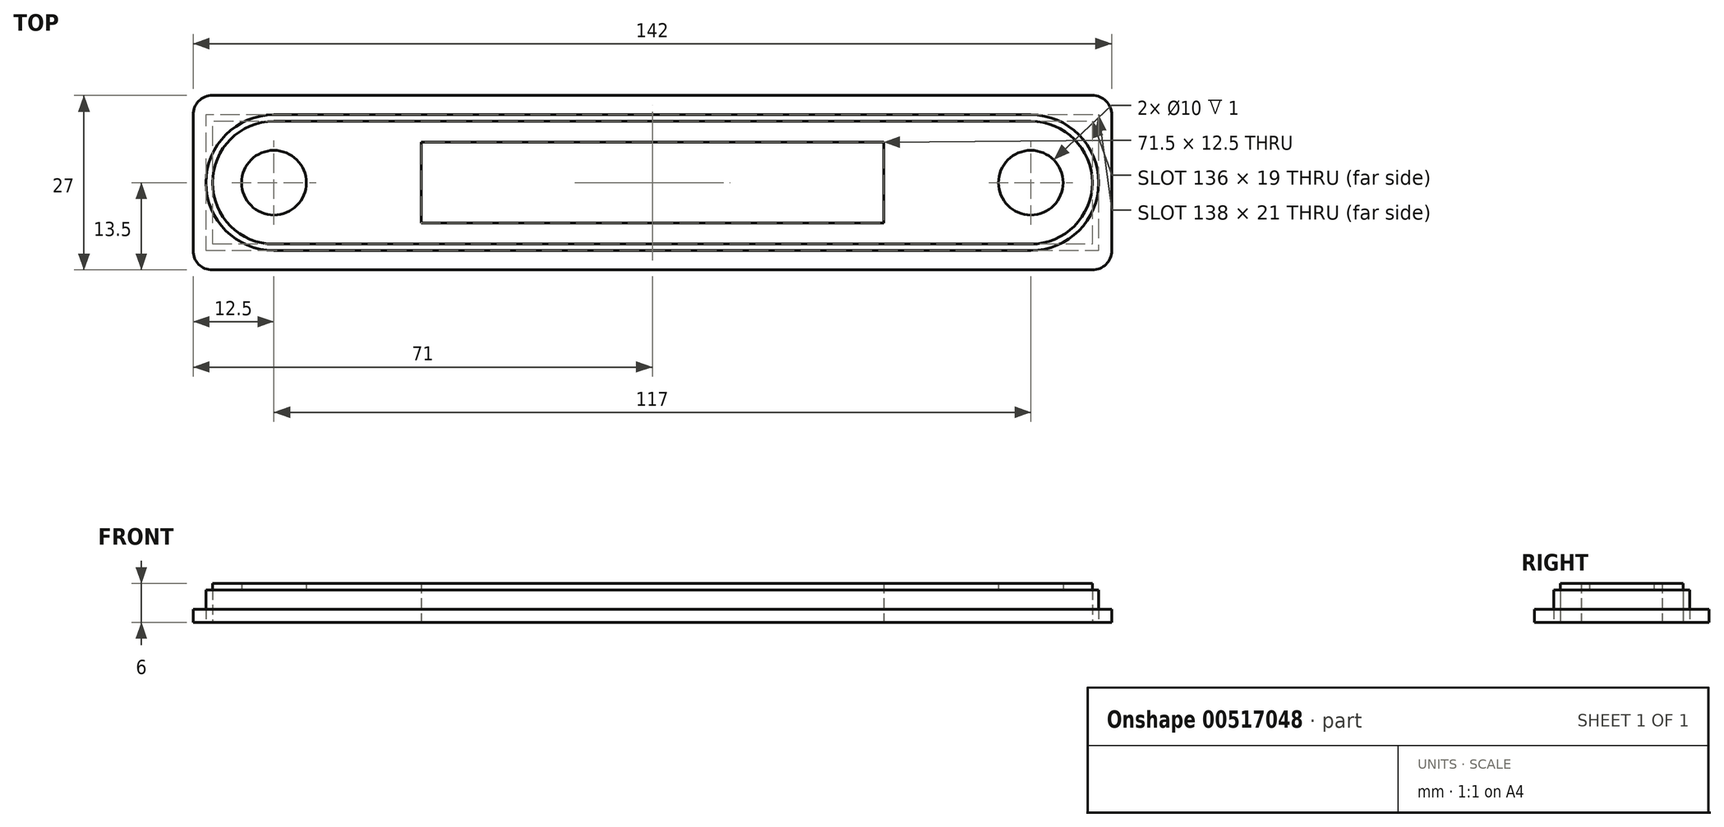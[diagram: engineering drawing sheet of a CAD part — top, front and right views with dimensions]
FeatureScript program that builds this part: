
annotation { "Feature Type Name" : "Feature", "Feature Type Description" : "" }
export const myFeature = defineFeature(function(context is Context, id is Id, definition is map)
    precondition{}
    {
        {
            var Q0;
            Q0=qCreatedBy(makeId("Top.planeOp"),FACE);
            var sketch = newSketch(context, id + "F0", { "sketchPlane" : qUnion([Q0])});
            skArc(sketch, "E0", {"start": v(-58.5, 5) * mm, "mid": v(-62.04, 3.54) * mm, "end": v(-63.5, 0) * mm});
            skArc(sketch, "E1", {"start": v(-63.5, 0) * mm, "mid": v(-62.04, -3.54) * mm, "end": v(-58.5, -5) * mm});
            skArc(sketch, "E2", {"start": v(-58.5, -5) * mm, "mid": v(-54.96, -3.54) * mm, "end": v(-53.5, 0) * mm});
            skArc(sketch, "E3", {"start": v(-53.5, 0) * mm, "mid": v(-54.96, 3.54) * mm, "end": v(-58.5, 5) * mm});
            skArc(sketch, "E4", {"start": v(58.5, 5) * mm, "mid": v(54.96, 3.54) * mm, "end": v(53.5, 0) * mm});
            skArc(sketch, "E5", {"start": v(53.5, 0) * mm, "mid": v(54.96, -3.54) * mm, "end": v(58.5, -5) * mm});
            skArc(sketch, "E6", {"start": v(58.5, -5) * mm, "mid": v(62.04, -3.54) * mm, "end": v(63.5, 0) * mm});
            skArc(sketch, "E7", {"start": v(63.5, 0) * mm, "mid": v(62.04, 3.54) * mm, "end": v(58.5, 5) * mm});
            skLineSegment(sketch, "E8", {"start": v(-58.5, -10.5) * mm, "end": v(58.5, -10.5) * mm});
            skArc(sketch, "E9", {"start": v(58.5, -10.5) * mm, "mid": v(65.92, -7.42) * mm, "end": v(69, 0) * mm});
            skArc(sketch, "E10", {"start": v(69, 0) * mm, "mid": v(65.92, 7.42) * mm, "end": v(58.5, 10.5) * mm});
            skLineSegment(sketch, "E11", {"start": v(58.5, 10.5) * mm, "end": v(-58.5, 10.5) * mm});
            skArc(sketch, "E12", {"start": v(-58.5, 10.5) * mm, "mid": v(-65.92, 7.42) * mm, "end": v(-69, 0) * mm});
            skArc(sketch, "E13", {"start": v(-69, 0) * mm, "mid": v(-65.92, -7.42) * mm, "end": v(-58.5, -10.5) * mm});
            skLineSegment(sketch, "E14", {"start": v(-35.75, -6.25) * mm, "end": v(35.75, -6.25) * mm});
            skLineSegment(sketch, "E15", {"start": v(35.75, -6.25) * mm, "end": v(35.75, 6.25) * mm});
            skLineSegment(sketch, "E16", {"start": v(35.75, 6.25) * mm, "end": v(-35.75, 6.25) * mm});
            skLineSegment(sketch, "E17", {"start": v(-35.75, 6.25) * mm, "end": v(-35.75, -6.25) * mm});
            skArc(sketch, "E18", {"start": v(-71, -10.5) * mm, "mid": v(-70.12, -12.62) * mm, "end": v(-68, -13.5) * mm});
            skLineSegment(sketch, "E19", {"start": v(-68, -13.5) * mm, "end": v(68, -13.5) * mm});
            skArc(sketch, "E20", {"start": v(68, -13.5) * mm, "mid": v(70.12, -12.62) * mm, "end": v(71, -10.5) * mm});
            skLineSegment(sketch, "E21", {"start": v(71, -10.5) * mm, "end": v(71, 10.5) * mm});
            skArc(sketch, "E22", {"start": v(71, 10.5) * mm, "mid": v(70.12, 12.62) * mm, "end": v(68, 13.5) * mm});
            skLineSegment(sketch, "E23", {"start": v(68, 13.5) * mm, "end": v(-68, 13.5) * mm});
            skArc(sketch, "E24", {"start": v(-68, 13.5) * mm, "mid": v(-70.12, 12.62) * mm, "end": v(-71, 10.5) * mm});
            skLineSegment(sketch, "E25", {"start": v(-71, 10.5) * mm, "end": v(-71, -10.5) * mm});
            skLineSegment(sketch, "E26", {"start": v(-58.5, -9.5) * mm, "end": v(58.5, -9.5) * mm});
            skArc(sketch, "E27", {"start": v(58.5, -9.5) * mm, "mid": v(65.22, -6.72) * mm, "end": v(68, 0) * mm});
            skArc(sketch, "E28", {"start": v(68, 0) * mm, "mid": v(65.22, 6.72) * mm, "end": v(58.5, 9.5) * mm});
            skLineSegment(sketch, "E29", {"start": v(58.5, 9.5) * mm, "end": v(-58.5, 9.5) * mm});
            skArc(sketch, "E30", {"start": v(-58.5, 9.5) * mm, "mid": v(-65.22, 6.72) * mm, "end": v(-68, 0) * mm});
            skArc(sketch, "E31", {"start": v(-68, 0) * mm, "mid": v(-65.22, -6.72) * mm, "end": v(-58.5, -9.5) * mm});
            skSolve(sketch);
        }
        {
            var Q0;
            Q0=makeQuery(id+"F0.imprint","IMPRINT",FACE,{"disambiguationData":[TD([[makeQuery(id+"F0.imprint","IMPRINT",EDGE,{"derivedFrom":sQuery(id+"F0.wireOp",EDGE,"E8")}),-1.0]])]});
            extrude(context, id + "F1", {"entities" : qUnion([Q0]), "depth" : 2 * mm, "offsetDistance" : 25 * mm});
        }
        {
            var Q0;
            Q0=makeQuery(id+"F0.imprint","IMPRINT",FACE,{"disambiguationData":[TD([[makeQuery(id+"F0.imprint","IMPRINT",EDGE,{"derivedFrom":sQuery(id+"F0.wireOp",EDGE,"E0")}),-1.0]])]});
            extrude(context, id + "F2", {"entities" : qUnion([Q0]), "depth" : 6 * mm, "offsetDistance" : 25 * mm});
        }
        {
            var Q0;
            Q0=makeQuery(id+"F0.imprint","IMPRINT",FACE,{"disambiguationData":[TD([[makeQuery(id+"F0.imprint","IMPRINT",EDGE,{"derivedFrom":sQuery(id+"F0.wireOp",EDGE,"E8")}),1.0]])]});
            extrude(context, id + "F3", {"entities" : qUnion([Q0]), "depth" : 5 * mm, "offsetDistance" : 25 * mm});
        }
        {
            var Q0;
            Q0=makeQuery(id+"F0.imprint","IMPRINT",FACE,{"disambiguationData":[TD([[makeQuery(id+"F0.imprint","IMPRINT",EDGE,{"derivedFrom":sQuery(id+"F0.wireOp",EDGE,"E0")}),1.0]])]});
            var Q1;
            Q1=makeQuery(id+"F0.imprint","IMPRINT",FACE,{"disambiguationData":[TD([[makeQuery(id+"F0.imprint","IMPRINT",EDGE,{"derivedFrom":sQuery(id+"F0.wireOp",EDGE,"E4")}),1.0]])]});
            extrude(context, id + "F4", {"entities" : qUnion([Q0, Q1]), "operationType" : NewBodyOperationType.ADD, "depth" : 5 * mm, "offsetDistance" : 25 * mm});
        }
    });
